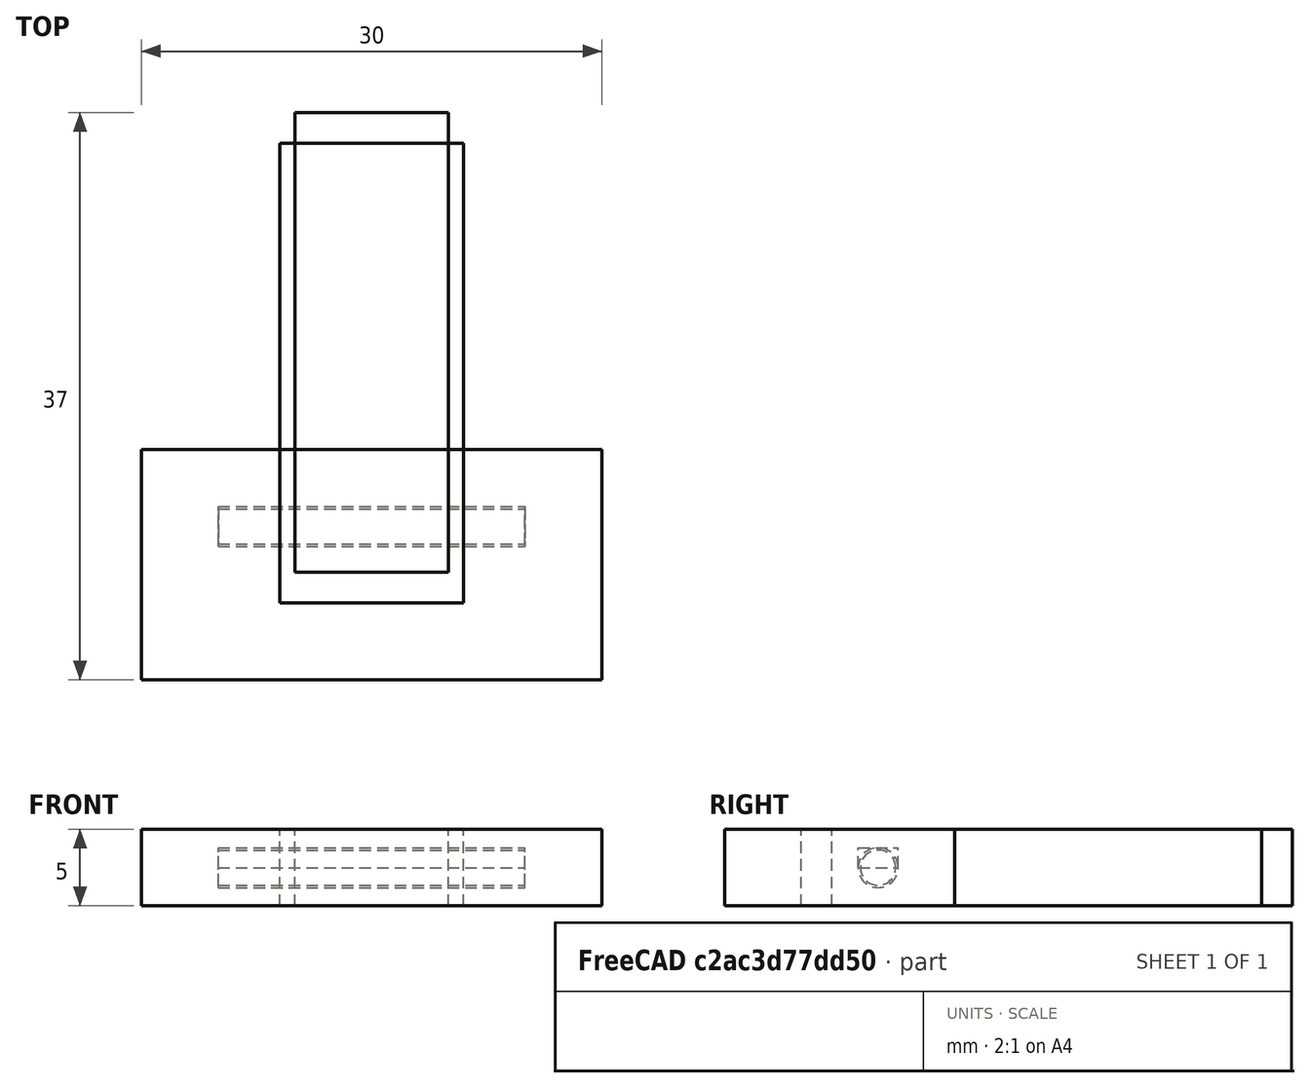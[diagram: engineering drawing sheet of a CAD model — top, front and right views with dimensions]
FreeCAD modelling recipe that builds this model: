
FCSTD DOCUMENT  (FreeCAD 0.18R16146 (Git))
Label: Hinge
License: All rights reserved
LicenseURL: http://en.wikipedia.org/wiki/All_rights_reserved
objects: Part::Box×4, Part::Cylinder×2
note: 6 computed .brp shape members not serialized (recipe doc carries the construction recipe); baked Part::Feature solids carry a one-line shape summary decoded from their .brp

FEATURE [Part::Box] Box  label="Cube"
  AttacherType = Attacher::AttachEngine3D
  Height = 5
  Length = 30
  Placement = pos=(0,-10,-2.5) rot=(0,0,1;0rad)
  Width = 15
FEATURE [Part::Box] Box001  label="Cube001"
  AttacherType = Attacher::AttachEngine3D
  Height = 5
  Length = 10
  Placement = pos=(10,-3,-2.5) rot=(0,0,1;0rad)
  Width = 30
FEATURE [Part::Cylinder] Cylinder
  Angle = 360
  AttacherType = Attacher::AttachEngine3D
  Height = 20
  Placement = pos=(5,0,0) rot=(0,1,0;1.5708rad)
  Radius = 1.15
FEATURE [Part::Cylinder] Cylinder001
  Angle = 360
  AttacherType = Attacher::AttachEngine3D
  Height = 20
  Placement = pos=(5,0,0) rot=(0,1,0;1.5708rad)
  Radius = 1.3
FEATURE [Part::Box] Box002  label="Cube002"
  AttacherType = Attacher::AttachEngine3D
  Height = 1.3
  Length = 20
  Placement = pos=(5,-1.3,0) rot=(0,0,1;0rad)
  Width = 2.6
FEATURE [Part::Box] Box003  label="Cube003"
  AttacherType = Attacher::AttachEngine3D
  Height = 5
  Length = 12
  Placement = pos=(9,-5,-2.5) rot=(0,0,1;0rad)
  Width = 30
